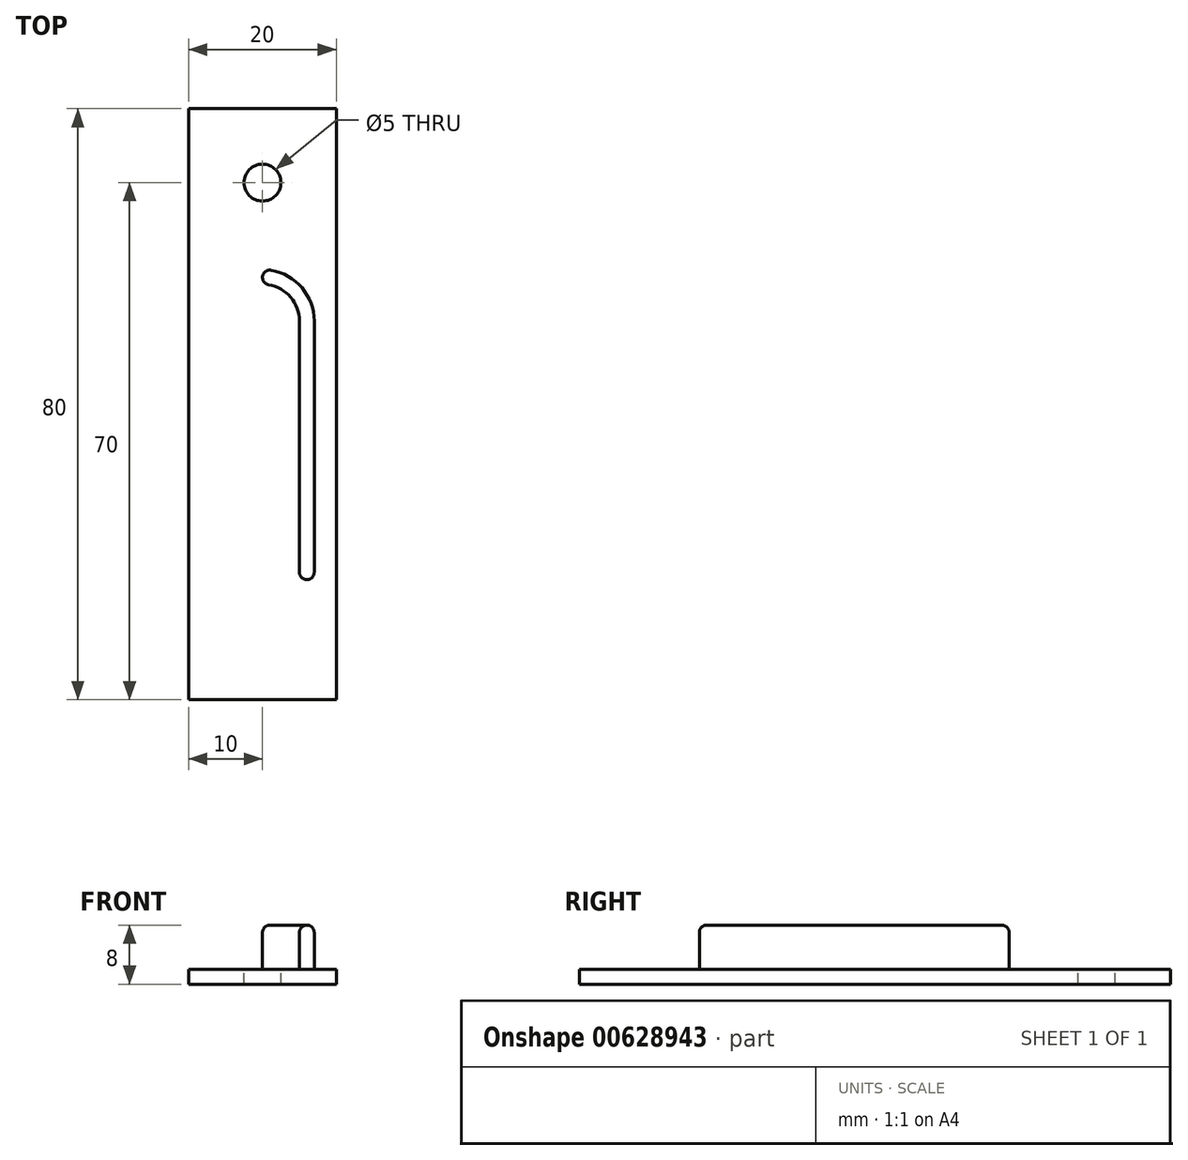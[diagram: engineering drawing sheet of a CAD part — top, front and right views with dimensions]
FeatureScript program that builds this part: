
annotation { "Feature Type Name" : "Feature", "Feature Type Description" : "" }
export const myFeature = defineFeature(function(context is Context, id is Id, definition is map)
    precondition{}
    {
        {
            var Q0;
            Q0=qCreatedBy(makeId("Top.planeOp"),FACE);
            var sketch = newSketch(context, id + "F0", { "sketchPlane" : qUnion([Q0])});
            skLineSegment(sketch, "E0.bottom", {"start": v(10, -40) * mm, "end": v(-10, -40) * mm});
            skLineSegment(sketch, "E0.top", {"start": v(10, 40) * mm, "end": v(-10, 40) * mm});
            skLineSegment(sketch, "E0.left", {"start": v(10, -40) * mm, "end": v(10, 40) * mm});
            skLineSegment(sketch, "E0.right", {"start": v(-10, -40) * mm, "end": v(-10, 40) * mm});
            skPoint(sketch, "E0.middle", {"position": v(0, 0) * mm});
            skSolve(sketch);
        }
        {
            var Q0;
            Q0=makeQuery(id+"F0.imprint","IMPRINT",FACE,{"disambiguationData":[TD([[makeQuery(id+"F0.imprint","IMPRINT",EDGE,{"derivedFrom":sQuery(id+"F0.wireOp",EDGE,"E0.bottom")}),-1.0]])]});
            extrude(context, id + "F1", {"entities" : qUnion([Q0]), "oppositeDirection" : true, "depth" : 2 * mm, "offsetDistance" : 25 * mm});
        }
        {
            var Q0;
            Q0=qCreatedBy(makeId("Top.planeOp"),FACE);
            var sketch = newSketch(context, id + "F2", { "sketchPlane" : qUnion([Q0])});
            skArc(sketch, "E1", {"start": v(5, 11.25) * mm, "mid": v(3.54, 14.78) * mm, "end": v(0, 16.25) * mm});
            skLineSegment(sketch, "E2", {"start": v(5, 11.25) * mm, "end": v(5, -23.75) * mm});
            skPoint(sketch, "E3.start.orphan", {"position": v(0, 16.25) * mm});
            skPoint(sketch, "E4.start.orphan", {"position": v(3, 11.25) * mm});
            skPoint(sketch, "E5.start.orphan", {"position": v(4.5, -23.75) * mm});
            skLineSegment(sketch, "E6", {"start": v(4.5, -23.75) * mm, "end": v(5, -23.75) * mm});
            skPoint(sketch, "E7.orphan", {"position": v(3, -23.75) * mm});
            skArc(sketch, "E8", {"start": v(7, 11.25) * mm, "mid": v(4.95, 16.2) * mm, "end": v(0, 18.25) * mm});
            skLineSegment(sketch, "E9", {"start": v(0, 16.25) * mm, "end": v(0, 18.25) * mm});
            skLineSegment(sketch, "E10", {"start": v(7, 11.25) * mm, "end": v(7, -23.75) * mm});
            skLineSegment(sketch, "E11", {"start": v(7, -23.75) * mm, "end": v(5, -23.75) * mm});
            skSolve(sketch);
        }
        {
            var Q0;
            Q0=makeQuery(id+"F2.imprint","IMPRINT",FACE,{"disambiguationData":[TD([[makeQuery(id+"F2.imprint","IMPRINT",EDGE,{"derivedFrom":sQuery(id+"F2.wireOp",EDGE,"E1")}),-1.0]])]});
            extrude(context, id + "F3", {"entities" : qUnion([Q0]), "operationType" : NewBodyOperationType.ADD, "depth" : 6 * mm, "offsetDistance" : 25 * mm});
        }
        {
            var Q0;
            Q0=makeQuery(id+"F3.opExtrude","CAP_EDGE",EDGE,{"disambiguationData":[OSD([sQuery(id+"F2.wireOp",EDGE,"E9")])],"isStart":false});
            fillet(context, id + "F4", {"entities" : qUnion([Q0]), "radius" : 1 * mm, "tangentPropagation" : true, "allowEdgeOverflow" : false});
        }
        {
            var Q0;
            Q0=makeQuery(id+"F3.opExtrude","CAP_EDGE",EDGE,{"disambiguationData":[OSD([sQuery(id+"F2.wireOp",EDGE,"E11")])],"isStart":false});
            var Q1;
            Q1=makeQuery(id+"F3.opExtrude","CAP_EDGE",EDGE,{"disambiguationData":[OSD([sQuery(id+"F2.wireOp",EDGE,"E1")])],"isStart":false});
            fillet(context, id + "F5", {"entities" : qUnion([Q0, Q1]), "radius" : 1 * mm, "tangentPropagation" : true, "allowEdgeOverflow" : false});
        }
        {
            var Q0;
            Q0=makeQuery(id+"F3.opExtrude","CAP_EDGE",EDGE,{"disambiguationData":[OSD([sQuery(id+"F2.wireOp",EDGE,"E10")])],"isStart":false});
            fillet(context, id + "F6", {"entities" : qUnion([Q0]), "radius" : 1 * mm, "tangentPropagation" : true, "allowEdgeOverflow" : false});
        }
        {
            var Q0;
            Q0=qCreatedBy(makeId("Top.planeOp"),FACE);
            var sketch = newSketch(context, id + "F7", { "sketchPlane" : qUnion([Q0])});
            skCircle(sketch, "E12", {"center": v(0, 30) * mm, "radius": 2.5 * mm});
            skCircle(sketch, "E13.MirrorC", {"center": v(0, -30) * mm, "radius": 2.5 * mm});
            skSolve(sketch);
        }
        {
            var Q0;
            Q0=makeQuery(id+"F7.imprint","IMPRINT",FACE,{"disambiguationData":[TD([[makeQuery(id+"F7.imprint","IMPRINT",EDGE,{"derivedFrom":sQuery(id+"F7.wireOp",EDGE,"E12")}),1.0]])]});
            var Q1;
            Q1=makeQuery(id+"F7.imprint","IMPRINT",FACE,{"disambiguationData":[TD([[makeQuery(id+"F7.imprint","IMPRINT",EDGE,{"derivedFrom":sQuery(id+"F7.wireOp",EDGE,"E13.MirrorC")}),-1.0]])]});
            extrude(context, id + "F8", {"entities" : qUnion([Q0, Q1]), "operationType" : NewBodyOperationType.REMOVE, "oppositeDirection" : true, "depth" : 5 * mm, "offsetDistance" : 25 * mm});
        }
        {
            var Q0;
            Q0=makeQuery(id+"F3.opExtrude","SWEPT_EDGE",EDGE,{"disambiguationData":[OSD([sQuery(id+"F2.wireOp",EDGE,"E2"),sQuery(id+"F2.wireOp",EDGE,"E11")])]});
            fillet(context, id + "F9", {"entities" : qUnion([Q0]), "radius" : 1 * mm, "tangentPropagation" : true, "allowEdgeOverflow" : false});
        }
    });
